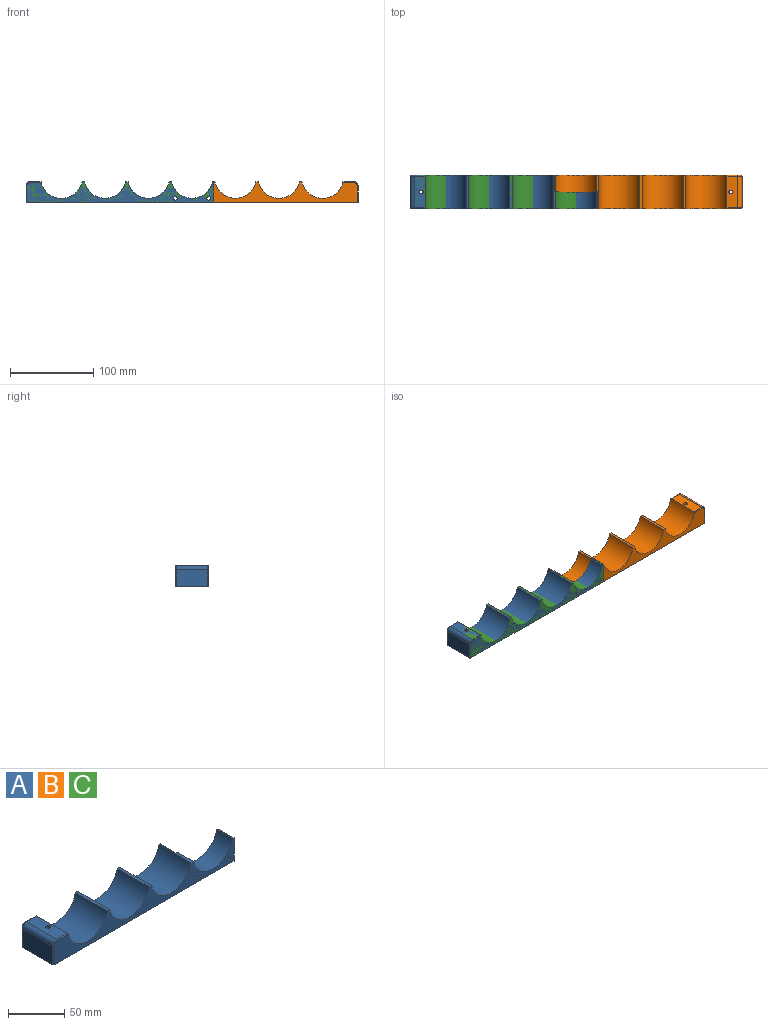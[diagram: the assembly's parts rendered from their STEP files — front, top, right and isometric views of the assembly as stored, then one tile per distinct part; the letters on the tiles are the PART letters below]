
ASSEMBLY  parts=3 mates=1
PART A: 27 faces, bbox 226.6x40x25.4 mm
  f0: plane 38x13.1mm, normal (0,0,1), area 481.9mm2, adj f9,f16,f19,f21,f25
  f1: plane 40x3mm, normal (0,0,1), area 120.1mm2, adj f5,f7,f15,f16
  f2: plane 40x3mm, normal (0,0,1), area 120.1mm2, adj f5,f7,f14,f15
  f3: plane 40x3mm, normal (0,0,1), area 86.1mm2, adj f4,f5,f7,f10,f13,f14
  f4: plane 25x20mm, normal (1,0,0), area 500mm2, adj f3,f5,f10,f12
  f5: plane 172.6x25mm, normal (0,1,0), area 2052.8mm2, adj f1,f2,f3,f4,f12,f14,f15,f16
  f6: plane 38x20mm, normal (-1,0,0), area 760mm2, adj f12,f19,f22,f24
  f7: plane 225.2x25mm, normal (0,-1,0), area 2588.8mm2, adj f1,f2,f3,f8,f11,f12,f13,f14
  f8: plane 25x19mm, normal (1,0,0), area 475mm2, adj f7,f11,f12,f20
  f9: cylinder r=2.25mm len=25mm, axis (0,0,-1), area 353.4mm2, adj f0,f12
  f10: plane 51.6x25mm, normal (0,1,0), area 511mm2, adj f3,f4,f11,f12,f13,f17,f18,f20
  f11: plane 20x1.5mm, normal (0,0,1), area 29.8mm2, adj f7,f8,f10,f13,f20
  f12: plane 226.2x40mm, normal (0,0,-1), area 7979.5mm2, adj f4,f5,f6,f7,f8,f9,f10,f20
  f13: cylinder r=25.2mm len=49.4mm, axis (0,-1,0), area 1382mm2, adj f3,f7,f10,f11
  f14: cylinder r=25.2mm len=49.4mm, axis (0,-1,0), area 2764.1mm2, adj f2,f3,f5,f7
  f15: cylinder r=25.2mm len=49.4mm, axis (0,-1,0), area 2764.1mm2, adj f1,f2,f5,f7
  f16: cylinder r=25.2mm len=49.4mm, axis (0,-1,0), area 2763.6mm2, adj f0,f1,f5,f7,f21,f25
  f17: cylinder r=2.25mm len=20mm, axis (0,1,0), area 282.7mm2, adj f7,f10
  f18: cylinder r=2.25mm len=20mm, axis (0,1,0), area 282.7mm2, adj f7,f10
  f19: cylinder r=5mm len=38mm, axis (0,1,0), area 298.5mm2, adj f0,f6,f23,f26
  f20: cylinder r=1mm len=25mm, axis (0,0,1), area 39.3mm2, adj f8,f10,f11,f12
  f21: cylinder r=1mm len=13.32mm, axis (-1,0,0), area 20.7mm2, adj f0,f7,f16,f23
  f22: cylinder r=1mm len=20mm, axis (0,0,-1), area 31.4mm2, adj f6,f7,f12,f23
  f23: torus R=4mm, axis (0,-1,0), area 11.4mm2, adj f7,f19,f21,f22
  f24: cylinder r=1mm len=20mm, axis (0,0,1), area 31.4mm2, adj f5,f6,f12,f26
  f25: cylinder r=1mm len=13.32mm, axis (1,0,0), area 20.7mm2, adj f0,f5,f16,f26
  f26: torus R=4mm, axis (0,-1,0), area 11.4mm2, adj f5,f19,f24,f25
PART B: same geometry as A
PART C: same geometry as A
PLACE A t=(-7.4,7.98,5.87)mm
PLACE B rot(axis=(0,0,1),180deg) t=(166.4,7.98,5.87)mm
PLACE C t=(-7.4,7.98,5.87)mm
MATE fastened B.f18 <-> A.f17  axis (0,-1,0) through (99.5,7.98,10.87)mm
